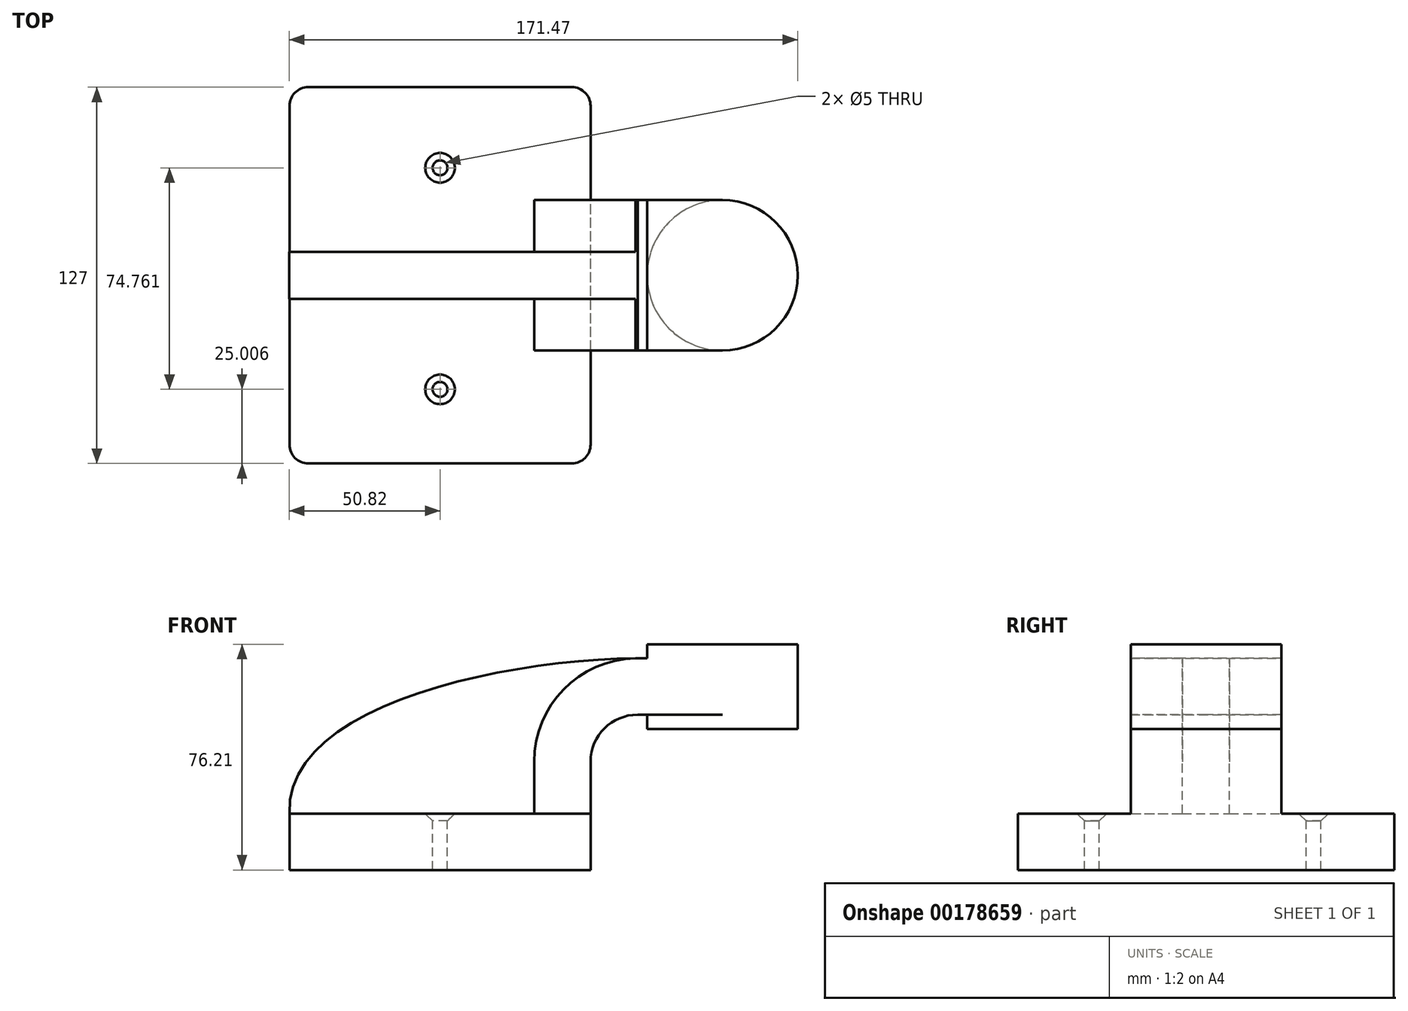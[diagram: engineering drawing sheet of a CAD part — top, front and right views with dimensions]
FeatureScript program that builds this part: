
annotation { "Feature Type Name" : "Feature", "Feature Type Description" : "" }
export const myFeature = defineFeature(function(context is Context, id is Id, definition is map)
    precondition{}
    {
        {
            var Q0;
            Q0=qCreatedBy(makeId("Front.planeOp"),FACE);
            var sketch = newSketch(context, id + "F0", { "sketchPlane" : qUnion([Q0])});
            skLineSegment(sketch, "E0.bottom", {"start": v(-50.8, 9.53) * mm, "end": v(50.8, 9.53) * mm});
            skLineSegment(sketch, "E0.top", {"start": v(-50.8, -9.52) * mm, "end": v(50.8, -9.52) * mm});
            skLineSegment(sketch, "E0.left", {"start": v(-50.8, 9.53) * mm, "end": v(-50.8, -9.52) * mm});
            skLineSegment(sketch, "E0.right", {"start": v(50.8, 9.53) * mm, "end": v(50.8, -9.52) * mm});
            skPoint(sketch, "E0.middle", {"position": v(0, 0) * mm});
            skLineSegment(sketch, "E1.bottom", {"start": v(69.85, 38.1) * mm, "end": v(120.65, 38.1) * mm});
            skLineSegment(sketch, "E1.top", {"start": v(69.85, 66.68) * mm, "end": v(120.65, 66.68) * mm});
            skLineSegment(sketch, "E1.left", {"start": v(69.85, 38.1) * mm, "end": v(69.85, 66.67) * mm});
            skLineSegment(sketch, "E1.right", {"start": v(120.65, 38.1) * mm, "end": v(120.65, 66.68) * mm});
            skPoint(sketch, "E1.middle", {"position": v(95.25, 52.39) * mm});
            skLineSegment(sketch, "E2", {"start": v(50.8, 9.53) * mm, "end": v(50.8, 27) * mm});
            skArc(sketch, "E3", {"start": v(50.8, 27) * mm, "mid": v(55.45, 38.23) * mm, "end": v(66.68, 42.88) * mm});
            skLineSegment(sketch, "E4", {"start": v(66.68, 42.88) * mm, "end": v(95.25, 42.88) * mm});
            skLineSegment(sketch, "E5.0", {"start": v(66.68, 61.93) * mm, "end": v(69.85, 61.93) * mm});
            skArc(sketch, "E5.1", {"start": v(31.75, 27) * mm, "mid": v(41.98, 51.7) * mm, "end": v(66.68, 61.93) * mm});
            skLineSegment(sketch, "E5.2", {"start": v(31.75, 9.53) * mm, "end": v(31.75, 27) * mm});
            skFitSpline(sketch, "E6", {"points": [v(-50.8, 9.53) * mm, v(66.68, 61.93) * mm], "startDerivative": vector(-4.66, 109.12) * mm, "endDerivative": vector(139.03, 1.22) * mm});
            skLineSegment(sketch, "E7", {"start": v(95.25, 38.1) * mm, "end": v(95.25, 66.68) * mm});
            skSolve(sketch);
        }
        {
            var Q0;
            Q0=makeQuery(id+"F0.imprint","IMPRINT",FACE,{"disambiguationData":[TD([[makeQuery(id+"F0.imprint","IMPRINT",EDGE,{"derivedFrom":sQuery(id+"F0.wireOp",EDGE,"E0.top")}),1.0]])]});
            extrude(context, id + "F1", {"entities" : qUnion([Q0]), "endBound" : BoundingType.SYMMETRIC, "depth" : 127 * mm});
        }
        {
            var Q0;
            {var subQ1=sQuery(id+"F0.wireOp",EDGE,"E2");Q0=makeQuery(id+"F0.imprint","IMPRINT",FACE,{"disambiguationData":[TD([[makeQuery(id+"F0.imprint","IMPRINT",EDGE,{"derivedFrom":subQ1}),1.0]])]});}
            var Q1;
            {var subQ5=sQuery(id+"F0.wireOp",EDGE,"u4WxUPUE-TyTC-BTi3-BHjO-wgd8iughRyTL");Q1=makeQuery(id+"F0.imprint","IMPRINT",FACE,{"disambiguationData":[TD([[makeQuery(id+"F0.imprint","IMPRINT",EDGE,{"derivedFrom":subQ5}),1.0]])]});}
            var Q2;
            {var subQ0=sQuery(id+"F0.wireOp",EDGE,"E4");var subQ1=sQuery(id+"F0.wireOp",EDGE,"E1.left");var subQ2=makeQuery(id+"F0.imprint","INTERSECT",VERTEX,{"derivedFrom":[subQ1,subQ0]});Q2=makeQuery(id+"F0.imprint","IMPRINT",FACE,{"disambiguationData":[TD([[makeQuery(id+"F0.imprint","IMPRINT",EDGE,{"disambiguationData":[TD([[subQ2,-1.0]])],"derivedFrom":subQ1}),-1.0]])]});}
            extrude(context, id + "F2", {"entities" : qUnion([Q0, Q1, Q2]), "operationType" : NewBodyOperationType.ADD, "endBound" : BoundingType.SYMMETRIC, "depth" : 50.8 * mm});
        }
        {
            var Q0;
            {var subQ3=sQuery(id+"F0.wireOp",EDGE,"E5.2");Q0=makeQuery(id+"F0.imprint","IMPRINT",FACE,{"disambiguationData":[TD([[makeQuery(id+"F0.imprint","IMPRINT",EDGE,{"derivedFrom":subQ3}),1.0]])]});}
            extrude(context, id + "F3", {"entities" : qUnion([Q0]), "operationType" : NewBodyOperationType.ADD, "endBound" : BoundingType.SYMMETRIC, "depth" : 15.88 * mm});
        }
        {
            var Q0;
            {var subQ0=sQuery(id+"F0.wireOp",EDGE,"E1.right");Q0=makeQuery(id+"F0.imprint","IMPRINT",FACE,{"disambiguationData":[TD([[makeQuery(id+"F0.imprint","IMPRINT",EDGE,{"derivedFrom":subQ0}),1.0]])]});}
            var Q1;
            Q1=sQuery(id+"F0.wireOp",EDGE,"E7");
            revolve(context, id + "F4", {"operationType" : NewBodyOperationType.ADD, "entities" : qUnion([Q0]), "axis" : qUnion([Q1]), "revolveType" : RevolveType.FULL});
        }
        {
            var Q0;
            Q0=makeQuery(id+"F1.opExtrude","CAP_EDGE",EDGE,{"disambiguationData":[OSD([sQuery(id+"F0.wireOp",EDGE,"E0.right")])],"isStart":false});
            var Q1;
            Q1=makeQuery(id+"F1.opExtrude","CAP_EDGE",EDGE,{"disambiguationData":[OSD([sQuery(id+"F0.wireOp",EDGE,"E0.left")])],"isStart":false});
            var Q2;
            Q2=makeQuery(id+"F1.opExtrude","CAP_EDGE",EDGE,{"disambiguationData":[OSD([sQuery(id+"F0.wireOp",EDGE,"E0.left")])],"isStart":true});
            var Q3;
            Q3=makeQuery(id+"F1.opExtrude","CAP_EDGE",EDGE,{"disambiguationData":[OSD([sQuery(id+"F0.wireOp",EDGE,"E0.right")])],"isStart":true});
            fillet(context, id + "F5", {"entities" : qUnion([Q0, Q1, Q2, Q3]), "radius" : 6.35 * mm, "tangentPropagation" : true, "allowEdgeOverflow" : false});
        }
        {
            var Q0;
            {var subQ4=sQuery(id+"F0.wireOp",EDGE,"E0.bottom");var subQ5=sQuery(id+"F0.wireOp",EDGE,"E0.right");var subQ6=sQuery(id+"F0.wireOp",EDGE,"E0.left");Q0=makeQuery(id+"F3.boolean.opBoolean","SPLIT",FACE,{"disambiguationData":[TD([makeQuery(id+"F1.opExtrude","CAP_FACE",FACE,{"disambiguationData":[OSD([subQ4,sQuery(id+"F0.wireOp",EDGE,"E0.top"),subQ6,subQ5])],"isStart":true})])],"derivedFrom":makeQuery(id+"F1.opExtrude","SWEPT_FACE",FACE,{"disambiguationData":[OSD([subQ4])]})});}
            var sketch = newSketch(context, id + "F6", { "sketchPlane" : qUnion([Q0])});
            skPoint(sketch, "E8", {"position": v(0, 36.27) * mm});
            skPoint(sketch, "E9", {"position": v(0, -38.5) * mm});
            skSolve(sketch);
        }
        {
            var Q0;
            Q0=sQuery(id+"F6.wireOp",VERTEX,"E8");
            var Q1;
            Q1=sQuery(id+"F6.wireOp",VERTEX,"E9");
            var Q2;
            Q2=makeQuery(id+"F1.opExtrude","SWEPT_BODY",BODY,{"disambiguationData":[OSD([sQuery(id+"F0.wireOp",EDGE,"E0.bottom"),sQuery(id+"F0.wireOp",EDGE,"E0.top"),sQuery(id+"F0.wireOp",EDGE,"E0.left"),sQuery(id+"F0.wireOp",EDGE,"E0.right")])]});
            hole(context, id + "F7", {"style" : HoleStyle.C_SINK, "endStyle" : HoleEndStyle.THROUGH, "holeDiameter" : 5 * mm, "cSinkDiameter" : 10 * mm, "cSinkAngle" : 90 * degree, "locations" : qUnion([Q0, Q1]), "scope" : qUnion([Q2]), "isTappedThrough" : true});
        }
    });
